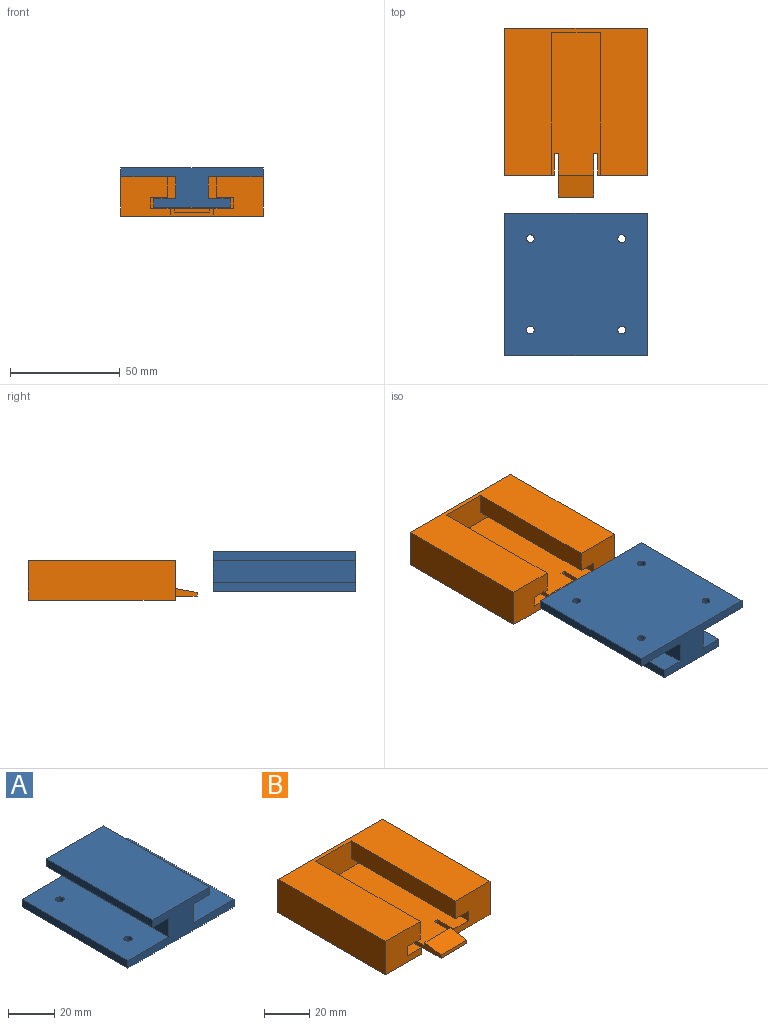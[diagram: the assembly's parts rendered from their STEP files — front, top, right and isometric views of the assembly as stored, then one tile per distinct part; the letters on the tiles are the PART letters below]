
ASSEMBLY  parts=2 mates=2
PART A: 18 faces, bbox 65x65x18 mm
  f0: plane 65x35mm, normal (0,0,1), area 2275mm2, adj f1,f7,f8,f9
  f1: plane 65x4mm, normal (-1,0,0), area 260mm2, adj f0,f2,f7,f8
  f2: plane 65x10mm, normal (0,0,-1), area 650mm2, adj f1,f3,f7,f8
  f3: plane 65x10mm, normal (-1,0,0), area 650mm2, adj f2,f4,f7,f8
  f4: plane 65x25mm, normal (0,0,1), area 1604.6mm2, adj f3,f5,f7,f8,f16,f17
  f5: plane 65x4mm, normal (-1,0,0), area 260mm2, adj f4,f6,f7,f8
  f6: plane 65x65mm, normal (0,0,-1), area 4184.3mm2, adj f5,f7,f8,f13,f14,f15,f16,f17
  f7: plane 65x18mm, normal (0,-1,0), area 550mm2, adj f0,f1,f2,f3,f4,f5,f6,f9
  f8: plane 65x18mm, normal (0,1,0), area 550mm2, adj f0,f1,f2,f3,f4,f5,f6,f9
  f9: plane 65x4mm, normal (1,0,0), area 260mm2, adj f0,f7,f8,f10
  f10: plane 65x10mm, normal (0,0,-1), area 650mm2, adj f7,f8,f9,f11
  f11: plane 65x10mm, normal (1,0,0), area 650mm2, adj f7,f8,f10,f12
  f12: plane 65x25mm, normal (0,0,1), area 1604.6mm2, adj f7,f8,f11,f13,f14,f15
  f13: plane 65x4mm, normal (1,0,0), area 260mm2, adj f6,f7,f8,f12
  f14: cylinder r=1.8mm len=4mm, axis (0,0,-1), area 45.2mm2, adj f6,f12
  f15: cylinder r=1.8mm len=4mm, axis (0,0,-1), area 45.2mm2, adj f6,f12
  f16: cylinder r=1.8mm len=4mm, axis (0,0,-1), area 45.2mm2, adj f4,f6
  f17: cylinder r=1.8mm len=4mm, axis (0,0,-1), area 45.2mm2, adj f4,f6
PART B: 24 faces, bbox 65x77x18 mm
  f0: plane 65x38mm, normal (0,0,1), area 2430mm2, adj f2,f3,f8,f9,f13,f15,f16,f17
  f1: plane 67x65mm, normal (0,0,-1), area 4155mm2, adj f2,f7,f8,f12,f14,f16,f17,f19
  f2: plane 22.5x18mm, normal (0,-1,0), area 350.6mm2, adj f0,f1,f3,f4,f5,f6,f7,f17
  f3: plane 65x5mm, normal (1,0,0), area 325mm2, adj f0,f2,f4,f13
  f4: plane 65x8.01mm, normal (0,0,-1), area 520.8mm2, adj f2,f3,f5,f13
  f5: plane 65x9.5mm, normal (1,0,0), area 617.5mm2, adj f2,f4,f6,f13
  f6: plane 67x65mm, normal (0,0,1), area 2926.6mm2, adj f2,f5,f7,f8,f11,f12,f13,f14
  f7: plane 67x18mm, normal (-1,0,0), area 1206mm2, adj f1,f2,f6,f14
  f8: plane 22.5x18mm, normal (0,-1,0), area 350.6mm2, adj f0,f1,f6,f9,f10,f11,f12,f16
  f9: plane 65x5mm, normal (-1,0,0), area 325mm2, adj f0,f8,f10,f13
  f10: plane 65x8.01mm, normal (0,0,-1), area 520.8mm2, adj f8,f9,f11,f13
  f11: plane 65x9.5mm, normal (-1,0,0), area 617.5mm2, adj f6,f8,f10,f13
  f12: plane 67x18mm, normal (1,0,0), area 1206mm2, adj f1,f6,f8,f14
  f13: plane 38x14.5mm, normal (0,-1,0), area 398.8mm2, adj f0,f3,f4,f5,f6,f9,f10,f11
  f14: plane 65x18mm, normal (0,1,0), area 1170mm2, adj f1,f6,f7,f12
  f15: plane 20x3.5mm, normal (1,0,0), area 43.8mm2, adj f0,f19,f20,f21,f22,f23
  f16: plane 10x3.5mm, normal (-1,0,0), area 35mm2, adj f0,f1,f8,f19
  f17: plane 10x3.5mm, normal (1,0,0), area 35mm2, adj f0,f1,f2,f19
  f18: plane 20x3.5mm, normal (-1,0,0), area 43.8mm2, adj f0,f19,f20,f21,f22,f23
  f19: plane 20x3.5mm, normal (0,-1,0), area 42mm2, adj f0,f1,f15,f16,f17,f18,f20
  f20: plane 20x16mm, normal (0,0,-1), area 320mm2, adj f15,f18,f19,f21
  f21: plane 16x1.75mm, normal (0,-1,0), area 28mm2, adj f15,f18,f20,f22
  f22: plane 16x10mm, normal (0,-0.17,0.99), area 162.4mm2, adj f15,f18,f21,f23
  f23: plane 16x1.75mm, normal (0,1,0), area 28mm2, adj f0,f15,f18,f22
PLACE A rot(axis=(1,0,0),180deg) t=(-10.83,-76.93,15.55)mm
PLACE B t=(-10.83,5.45,2.55)mm fixed
MATE planar A.f12 <-> B.f6  axis (0,0,-1) through (9.16,-76.93,20.55)mm
MATE planar A.f13 <-> B.f12  axis (1,0,0) through (21.67,-76.93,22.55)mm
